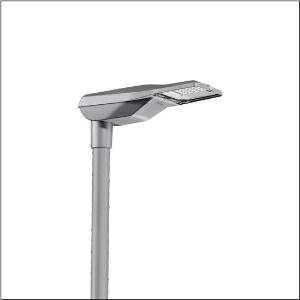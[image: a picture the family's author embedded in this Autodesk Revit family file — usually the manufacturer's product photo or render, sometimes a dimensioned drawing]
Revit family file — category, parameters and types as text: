
# Revit family: streetlight_sl_21_iq_micro___st1_5a_5xe1p41g08cb_60b9
name_source: partatom
category: Lighting Fixtures
units: mm (PartAtom-declared; Revit-internal decimal feet)

## family parameters
Cut with Voids When Loaded = No
Host = Face
Light Source = No
Part Type = Normal
Room Calculation Point = No
Round Connector Dimension = Use Diameter
Shared = No

## types (1)
- --- (1 x LED, 2930 lm, 19.4 W, 4000K)
    Apparent Load = 19 VA
    CIE Flux Codes = 22 53 95 100 100
    Color Rendering = 70
    Color Temperature = 4000K
    Default Elevation = 1800 mm
    Description = Streetlight SL 21 iQ micro, mast luminaire, primary light control with lens, of PMMA, primary optical cover: cover, of toughened safety glass, transparent, light distribution: ST1.5a, light emission: direct distribution, primary light characteristic: asymmetric, installation type: post-top, side-entry, LED, High Power LED, rated luminous flux: 2.930lm, luminous efficacy: 151lm/W, light colour: 740, colour temperature: 4000K, control gear: iQ Street-Remote, control: Street-Remote, Auto-Match, Temp-Guard, Lumen-Switch, Night-Set, Smart-Wire, Light-Fading, Desk-Remote (wireless, voltage-free reading and setting of iQ features in the workshop via application-optimized NFC function/RFID function), optimised constant luminous flux control (CLO 2.0), pre-setting: linear dimming characteristic, mains connection: 220..240V, AC, 50/60Hz, start of lifetime: 19W, end of service life: 20W, reduction: 10W, luminaire housing, of diecast aluminium, powder-coated, Siteco® metallic grey (DB 702S), corrosivity category C5 high according to DIN EN ISO 12944, please order mast flange separately, inclination adjustable: 0°, 5°, 10°, 15°, sealing non-destructively replaceable, multi-level sealing system, length: 528mm, width: 235mm, height: 110mm, mast flange for spigot size: 42mm (side-entry): 5XC10008XM4, 60/48mm (side-entry/post-top): 5XC10108XM2, 76/60mm (side-entry/post-top): 5XC10108XM1, protection rating (complete): IP66, insulation class (complete): insulation class II (safety insulation), certification: CE, ENEC, ENEC+, VDE, impact resistance: IK10, permissible operating ambient temperature for outdoor applications: -40..+50°C, standard-compliant lighting for roads and squares, packaging unit: 1 piece

Light Distribution: ST1.5a
    Height = 110 mm
    Lamp = 1 x LED
    Lamp Light Flux = 2930 lm
    Lamp Power = 19.4 W
    Lamp count = 1
    Length = 528 mm
    Luminous efficacy = 151 lm/W
    Manufacturer = Siteco
    ModVariant = No
    Model = 5XE1P41G08CB
    Number of Poles = 1
    OnlyDefault = Yes
    Power Factor = 1
    Product Name = Streetlight SL 21 iQ micro | ST1.5a
    Product group = mast luminaire | pylon top
    ProductGroupID = 6100
    Protection Class = Protection class II
    Protection Degree = IP 66
    RLX_Detail_Level = 1
    RLX_Emergency_Light_Flux = 0 lm
    RLX_Emergency_Type = 0
    RLX_Emergency_Type_DB = No
    RlxData = <blob elided: 102573 chars, md5=250dabde>
    Socket = socket
    Standby Power = 0 W
    System Light Flux = 2930 lm
    System Power = 19 W
    Type Comments = factory setting: luminous flux: 100 % | dim-lin: 254 | 387 mA
    Type Image = l_1006881.jpg
    URL = http://relux.com
    VarID = @adj_141277
    Voltage = 0 V
    Weight = 0.00 kg
    Width = 235 mm

## geometry (parser evidence)
native form markers: Blend x4, Sweep x11
no freeform markers — native parametric forms only
